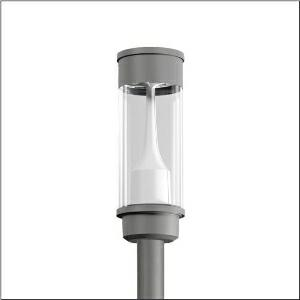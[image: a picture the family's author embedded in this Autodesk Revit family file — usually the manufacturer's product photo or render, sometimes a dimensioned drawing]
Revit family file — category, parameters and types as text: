
# Revit family: litepole_iq___pl1_2s_5xa5415rf14h_7319
name_source: partatom
category: Lighting Fixtures
units: mm (PartAtom-declared; Revit-internal decimal feet)

## family parameters
Cut with Voids When Loaded = No
Host = Face
Light Source = No
Part Type = Normal
Room Calculation Point = No
Round Connector Dimension = Use Diameter
Shared = No

## types (1)
- --- (1 x LED, 2970 lm, 18.5 W, 4000K)
    Apparent Load = 19 VA
    CIE Flux Codes = 23 62 94 96 100
    Color Rendering = 70
    Color Temperature = 4000K
    Default Elevation = 1800 mm
    Description = Litepole iQ, mast luminaire, Module 540 iQ-SR, primary light control with 3 zone facetted reflector, of plastic, silver coated, highly specular, structured, primary optical cover: cover, of PMMA, transparent, light distribution: PL1.2s, light emission: direct distribution, primary light characteristic: symmetric, installation type: post-top, LED, High Power LED, rated luminous flux: 2.970lm, luminous efficacy: 161lm/W, light colour: 740, colour temperature: 4000K, control gear: iQ Street-Remote, control: optimised constant luminous flux control (CLO 2.0), Desk-Remote (wireless, voltage-free reading and setting of iQ features in the workshop via application-optimized NFC function/RFID function), Light-Fading, Smart-Wire, Night-Set, Lumen-Switch, Temp-Guard, Auto-Match, Street-Remote, pre-setting: logarithmic dimming characteristic, with terminal, 6-pole, max. 2.5mm², mains connection: 230..240V, AC, 50/60Hz, start of lifetime: 19W, end of service life: 20W, reduction: 9W, luminaire housing, upper part, of glass-fibre reinforced polyester, coated, Siteco® metallic grey (DB 702S), diameter: 210mm, height: 590mm, spigot size: d x l = 76 x 70mm (post-top) | with reducer (optional accessory) 60 x 70mm, mounting height: 3..5m, post-top mast mounting element, of diecast aluminium, coated, Siteco® metallic grey (DB 702S), Module 540 iQ-SR, traffic white (RAL 9016), equipment: standard, protection rating (complete): IP65, insulation class (complete): insulation class II (safety insulation), certification: CE, ENEC, VDE, packaging unit: 1 piece

Light Distribution: PL1.2s
    Height = 590 mm
    Lamp = 1 x LED
    Lamp Light Flux = 2970 lm
    Lamp Power = 18.5 W
    Lamp count = 1
    Length = 220 mm
    Luminous efficacy = 161 lm/W
    Manufacturer = Siteco
    ModVariant = No
    Model = 5XA5415RF14H
    Number of Poles = 1
    OnlyDefault = Yes
    Power Factor = 1
    Product Name = Litepole iQ | PL1.2s
    Product group = mast luminaire | pylon top
    ProductGroupID = 6100
    Protection Class = Protection class II
    Protection Degree = IP 65
    RLX_Detail_Level = 1
    RLX_Emergency_Light_Flux = 0 lm
    RLX_Emergency_Type = 0
    RLX_Emergency_Type_DB = No
    RlxData = <blob elided: 25001 chars, md5=51e57f3e>
    Socket = socket
    Standby Power = 0 W
    System Light Flux = 2970 lm
    System Power = 19 W
    Type Comments = factory setting: luminous flux: 100 % | dim-lin: 254 | 385 mA
    Type Image = l_1006025.jpg
    URL = http://relux.com
    VarID = @adj_144792
    Voltage = 0 V
    Weight = 0.00 kg
    Width = 0 mm  [stored 0 ft]

note: [stored X ft] marks values corroborated as IEEE doubles in the binary element streams (Revit-internal decimal feet)

## geometry (parser evidence)
native form markers: Blend x4, Sweep x11
no freeform markers — native parametric forms only
